# Revit family: Domotics-DomesticRanges-GEWISS-CHORUS_DATA-SOCKET-OUTLET_TV+FM+SAT
name_source: partatom
category: Apparecchi elettrici
revit_build: Autodesk Revit 2016 (Build: 20161004_0715(x64)
units: mm (PartAtom-declared; Revit-internal decimal feet)

## family parameters
Condiviso = Sì
Host = Superficie
Mantenere orientamento annotazione = Sì
Punto di calcolo locali = Sì
Quota connettore circolare = Usa diametro
Taglio con vuoti quando caricato = Sì
Tipo di parte = Normale

## types (3) — shared parameters
Altezza_lampada = 45 mm  [stored 0.147638 ft]
Attenuation = 0 dB
Cable fixing = With screw
Case = Pressure casting zamak metal body
Catalogue = DOMOTICS
Catalogue Range = CHORUS - DOMESTIC RANGE
Category = TV/FM/SAT socket-outlet
Connectors = TV-FM-SAT
Description. = TV/FM/SAT socket-outlet
Description: = Direct
Electrocod = 0131
IDF = 85f33400-7a84-44aa-bdf3-e8dbde1c9c67
IDT = 87191e38-9908-47b3-89a1-3665361e7312
Immagine tipo = GW14382.jpg
Larghezza_lampada = 23 mm  [stored 0.0754593 ft]
No. Chorus modules: = 2
Produttore = GEWISS S.p.A.
Prospetto di default = 1219 mm
SEO = Socket outlet
Standard; = EN 60728-4; IEC 61169-2; IEC 61169-24
Technical sheet = https://www.gewiss.com
Tipo_ = CHORUS PRESE TV-FM-SAT : GW14382 Presa TV+FM+SAT 2M titanio
URL = https://www.gewiss.com
Version file RFA = 19.0
finitura = GEWISS NERO

## per-type parameters (varying)
| type | Colour | Descrizione | EAN code | Modello |
| GW14382 - TV+FM+SAT SOCKET 2M, TITANIUM | Titanium | TV+FM+SAT SOCKET 2M, TITANIUM | 8011564267077 | GW14382 |
| GW12382 - TV+FM+SAT SOCKET 2M BLACK | Black | TV+FM+SAT SOCKET 2M BLACK | 8011564269026 | GW12382 |
| GW10382 - TV+FM+SAT SOCKET, 2M WHITE | White | TV+FM+SAT SOCKET, 2M WHITE | 8011564257634 | GW10382 |

note: [stored X ft] marks values corroborated as IEEE doubles in the binary element streams (Revit-internal decimal feet)

## geometry (parser evidence)
native form markers: Sweep x2
no freeform markers — native parametric forms only
